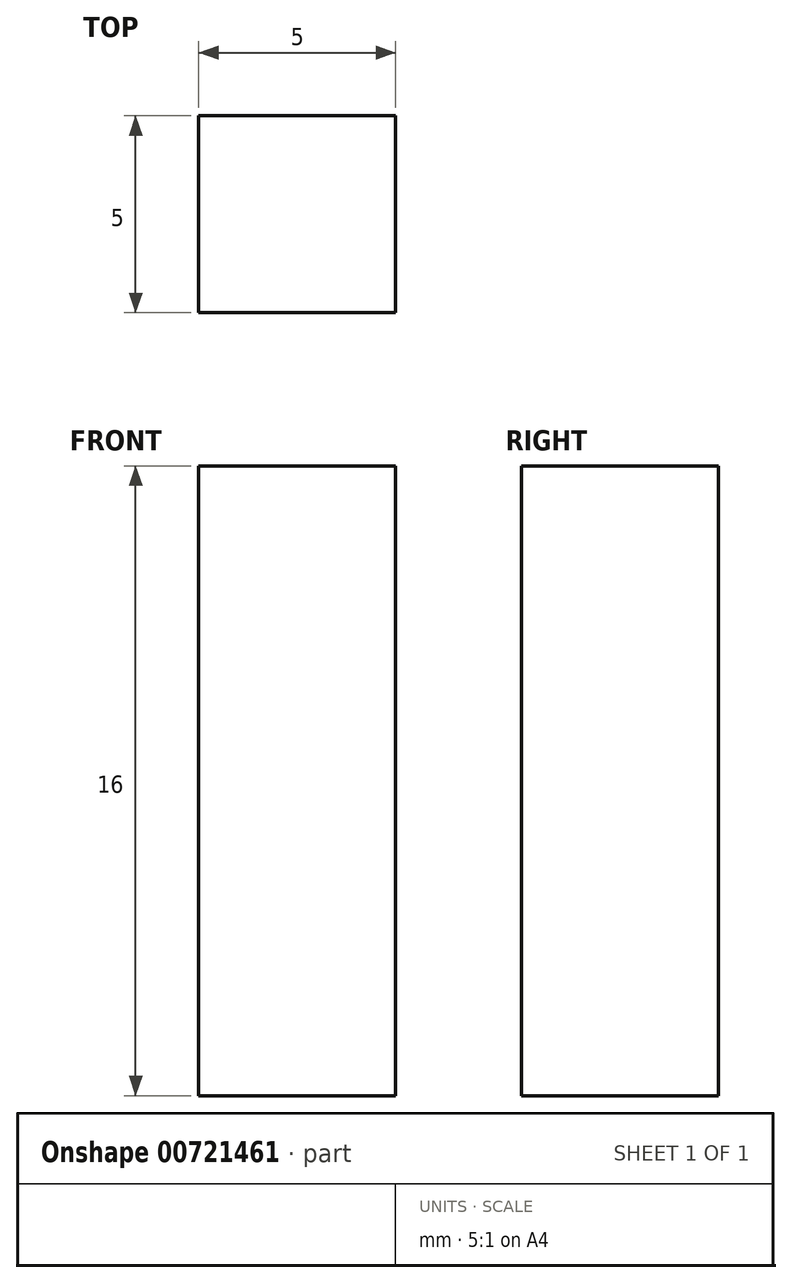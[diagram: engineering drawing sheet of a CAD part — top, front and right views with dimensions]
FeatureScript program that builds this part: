
annotation { "Feature Type Name" : "Feature", "Feature Type Description" : "" }
export const myFeature = defineFeature(function(context is Context, id is Id, definition is map)
    precondition{}
    {
        {
            var Q0;
            Q0=qCreatedBy(makeId("Top.planeOp"),FACE);
            var sketch = newSketch(context, id + "F0", { "sketchPlane" : qUnion([Q0])});
            skLineSegment(sketch, "E0.bottom", {"start": v(2.5, 2.5) * mm, "end": v(-2.5, 2.5) * mm});
            skLineSegment(sketch, "E0.top", {"start": v(2.5, -2.5) * mm, "end": v(-2.5, -2.5) * mm});
            skLineSegment(sketch, "E0.left", {"start": v(2.5, 2.5) * mm, "end": v(2.5, -2.5) * mm});
            skLineSegment(sketch, "E0.right", {"start": v(-2.5, 2.5) * mm, "end": v(-2.5, -2.5) * mm});
            skPoint(sketch, "E0.middle", {"position": v(0, 0) * mm});
            skSolve(sketch);
        }
        {
            var Q0;
            Q0=makeQuery(id+"F0.imprint","IMPRINT",FACE,{"disambiguationData":[TD([[makeQuery(id+"F0.imprint","IMPRINT",EDGE,{"derivedFrom":sQuery(id+"F0.wireOp",EDGE,"E0.bottom")}),1.0]])]});
            extrude(context, id + "F1", {"entities" : qUnion([Q0]), "depth" : 16 * mm, "offsetDistance" : 25.4 * mm});
        }
    });
